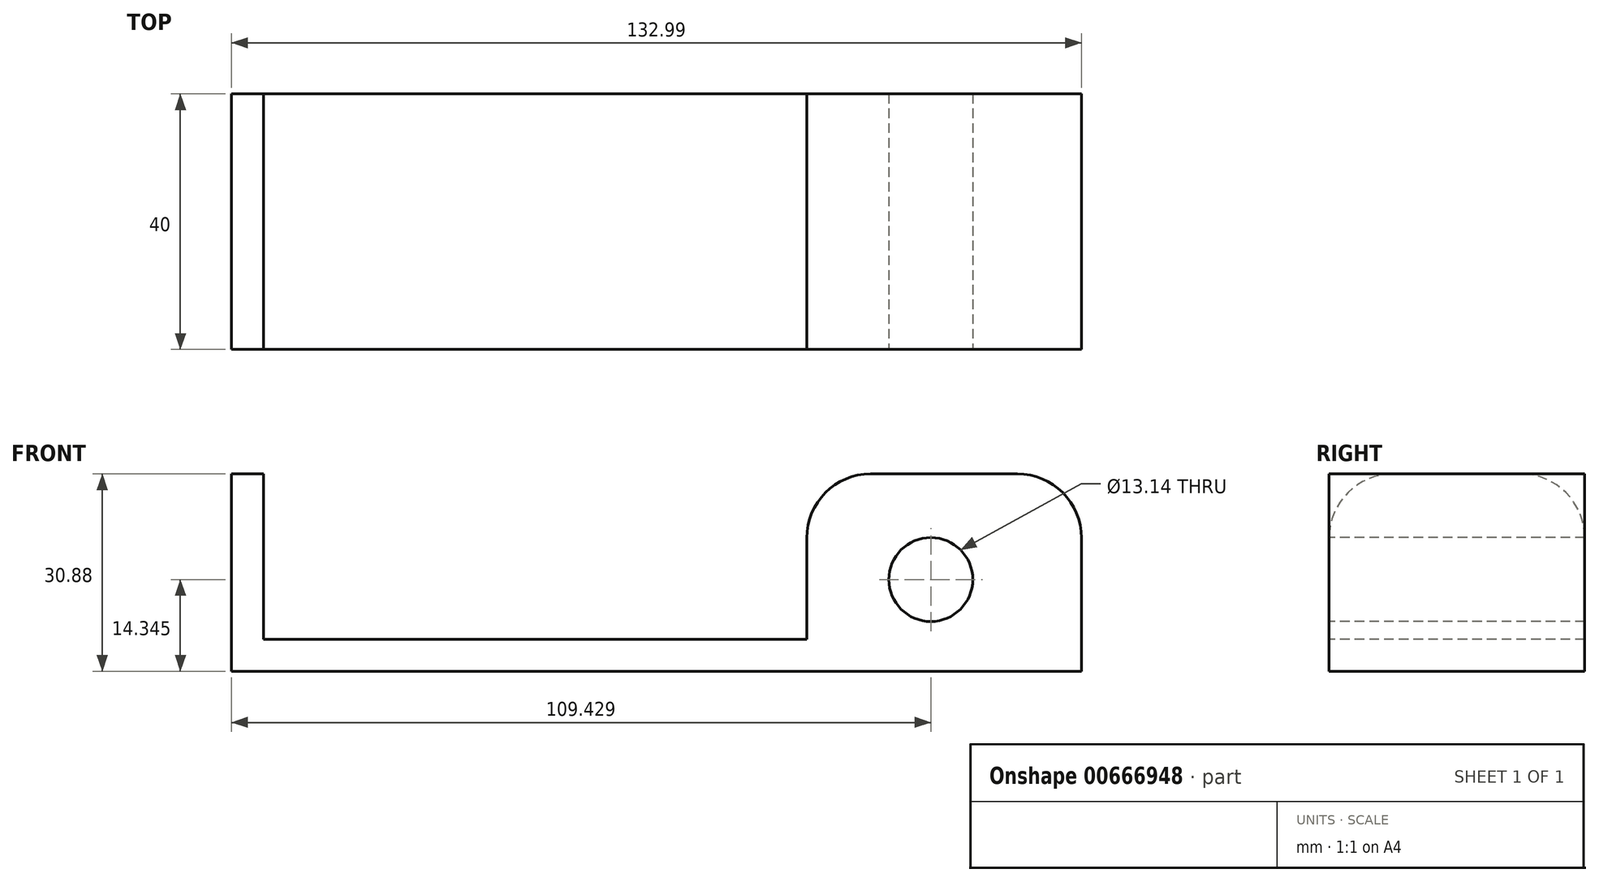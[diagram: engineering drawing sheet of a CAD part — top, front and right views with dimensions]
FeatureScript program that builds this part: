
annotation { "Feature Type Name" : "Feature", "Feature Type Description" : "" }
export const myFeature = defineFeature(function(context is Context, id is Id, definition is map)
    precondition{}
    {
        {
            var Q0;
            Q0=qCreatedBy(makeId("Front.planeOp"),FACE);
            var sketch = newSketch(context, id + "F0", { "sketchPlane" : qUnion([Q0])});
            skLineSegment(sketch, "E0", {"start": v(-52.72, 0) * mm, "end": v(37.28, 0) * mm});
            skLineSegment(sketch, "E1", {"start": v(37.28, 0) * mm, "end": v(37.28, 20.88) * mm});
            skLineSegment(sketch, "E2", {"start": v(47.28, 30.88) * mm, "end": v(70.27, 30.88) * mm});
            skLineSegment(sketch, "E3", {"start": v(80.27, 20.88) * mm, "end": v(80.27, 0) * mm});
            skLineSegment(sketch, "E4", {"start": v(-52.72, 0) * mm, "end": v(-52.72, 30.88) * mm});
            skLineSegment(sketch, "E5", {"start": v(37.28, 0) * mm, "end": v(80.27, 0) * mm});
            skLineSegment(sketch, "E6.0", {"start": v(-47.72, 5) * mm, "end": v(-47.72, 30.88) * mm});
            skLineSegment(sketch, "E6.1", {"start": v(-47.72, 5) * mm, "end": v(37.28, 5) * mm});
            skLineSegment(sketch, "E7", {"start": v(-52.72, 30.88) * mm, "end": v(-47.72, 30.88) * mm});
            skPoint(sketch, "E8.visualSharp", {"position": v(37.28, 30.88) * mm});
            skArc(sketch, "E8.filletArc", {"start": v(47.28, 30.88) * mm, "mid": v(40.21, 27.95) * mm, "end": v(37.28, 20.88) * mm});
            skPoint(sketch, "E9.visualSharp", {"position": v(80.27, 30.88) * mm});
            skArc(sketch, "E9.filletArc", {"start": v(80.27, 20.88) * mm, "mid": v(77.34, 27.95) * mm, "end": v(70.27, 30.88) * mm});
            skCircle(sketch, "E10", {"center": v(56.7, 14.34) * mm, "radius": 6.57 * mm});
            skSolve(sketch);
        }
        {
            var Q0;
            {var subQ1=sQuery(id+"F0.wireOp",EDGE,"E0");Q0=makeQuery(id+"F0.imprint","IMPRINT",FACE,{"disambiguationData":[TD([[makeQuery(id+"F0.imprint","IMPRINT",EDGE,{"derivedFrom":subQ1}),1.0]])]});}
            var Q1;
            Q1=makeQuery(id+"F0.imprint","IMPRINT",FACE,{"disambiguationData":[TD([[makeQuery(id+"F0.imprint","IMPRINT",EDGE,{"derivedFrom":sQuery(id+"F0.wireOp",EDGE,"E2")}),-1.0]])]});
            extrude(context, id + "F1", {"entities" : qUnion([Q0, Q1]), "endBound" : BoundingType.SYMMETRIC, "oppositeDirection" : true, "depth" : 40 * mm, "offsetDistance" : 25 * mm});
        }
        {
            var Q0;
            Q0=makeQuery(id+"F1.opExtrude","CAP_EDGE",EDGE,{"disambiguationData":[OSD([sQuery(id+"F0.wireOp",EDGE,"E7")])],"isStart":true});
            fillet(context, id + "F2", {"entities" : qUnion([Q0]), "radius" : 10 * mm, "tangentPropagation" : true, "allowEdgeOverflow" : false});
        }
        {
            var Q0;
            Q0=makeQuery(id+"F1.opExtrude","CAP_EDGE",EDGE,{"disambiguationData":[OSD([sQuery(id+"F0.wireOp",EDGE,"E7")])],"isStart":false});
            fillet(context, id + "F3", {"entities" : qUnion([Q0]), "radius" : 10 * mm, "tangentPropagation" : true, "allowEdgeOverflow" : false});
        }
    });
